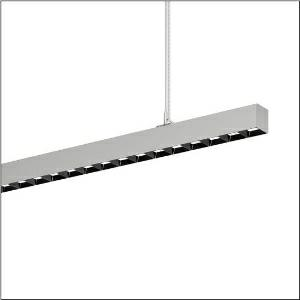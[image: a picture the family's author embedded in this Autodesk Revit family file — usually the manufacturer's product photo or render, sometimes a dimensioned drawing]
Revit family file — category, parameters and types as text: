
# Revit family: silica_21_51mx32tat7s
name_source: partatom
category: Lighting Fixtures
units: mm (PartAtom-declared; Revit-internal decimal feet)

## family parameters
Cut with Voids When Loaded = No
Host = Face
Light Source = No
Part Type = Normal
Room Calculation Point = No
Round Connector Dimension = Use Diameter
Shared = No

## types (1)
- --- (1 x LED, 6220 lm, 53.4 W, 6500K)
    Apparent Load = 53 VA
    CIE Flux Codes = 84 99 100 60 100
    Color Rendering = 80
    Color Temperature = 6500K
    Default Elevation = 1800 mm
    Description = Silica 21, office luminaire, primary light control with darklight reflector, of PMMA, black, CAT 2 (L<= 3000cd/m²), light emission: direct/indirect distribution, primary light characteristic: symmetric, installation type: suspended mounting, LED, rated luminous flux: 6.220lm, luminous efficacy: 111lm/W, light colour: 8tw, colour temperature: 2700..6500K, control gear: DALI DT8, with terminal, 3+2-pole, max. 2.5mm², mains connection: 220..240V, AC, 50/60Hz, rated input power: 56.1W, luminaire housing, of aluminium, metallic grey (RAL 9006), length: 1.204mm, width: 53mm, height: 53mm, protection rating (complete): IP20, insulation class (complete): insulation class I (protective earthing), certification: CE, permissible operating ambient temperature: 0..+35°C, standard: EN 50419, packaging unit: 1 piece
    Height = 53 mm
    Lamp = 1 x LED
    Lamp Light Flux = 6220 lm
    Lamp Power = 53.4 W
    Lamp count = 1
    Length = 1204 mm
    Luminous efficacy = 116 lm/W
    Manufacturer = Siteco
    ModVariant = No
    Model = 51MX32TAT7S
    Mounting Place = Ceiling
    Mounting Type = Pendant
    Number of Poles = 1
    OnlyDefault = Yes
    Power Factor = 1
    Product Name = Silica 21
    Product group = office luminaire | ceiling pendant
    ProductGroupID = 903
    Protection Class = Protection class I
    Protection Degree = IP 20
    RLX_Detail_Level = 1
    RLX_Emergency_Light_Flux = 0 lm
    RLX_Emergency_Type = 0
    RLX_Emergency_Type_DB = No
    RlxData = <blob elided: 41185 chars, md5=cf561ee9>
    Socket = socket
    Standby Power = 0 W
    System Light Flux = 6220 lm
    System Power = 53 W
    Type Comments = individual setting
    Type Image = l_1335859.jpg
    URL = http://relux.com
    VarID = @adj_139421
    Voltage = 0 V
    Weight = 0.00 kg
    Width = 53 mm

## geometry (parser evidence)
native form markers: Blend x4, Sweep x12
no freeform markers — native parametric forms only
